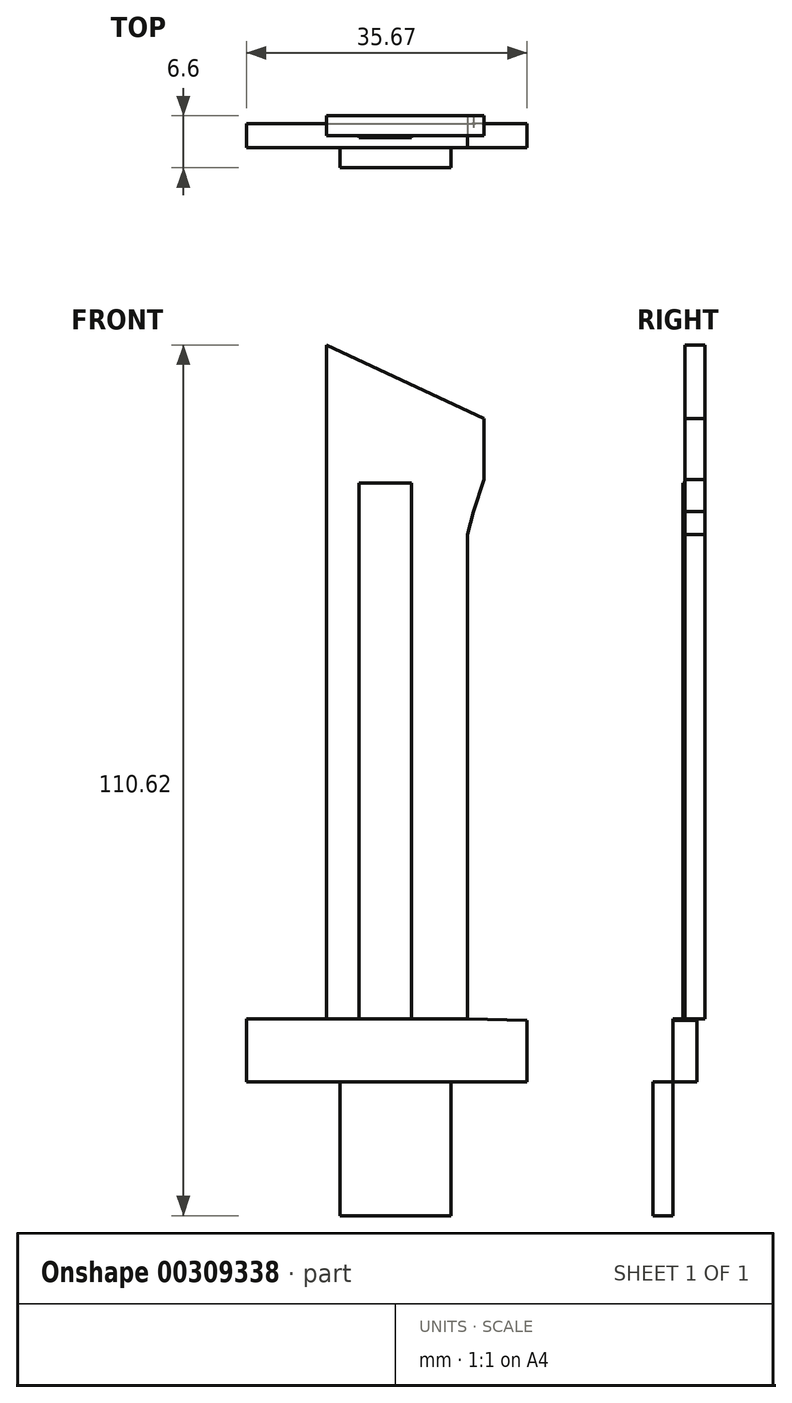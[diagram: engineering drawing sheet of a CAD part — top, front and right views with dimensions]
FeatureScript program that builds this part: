
annotation { "Feature Type Name" : "Feature", "Feature Type Description" : "" }
export const myFeature = defineFeature(function(context is Context, id is Id, definition is map)
    precondition{}
    {
        {
            var Q0;
            Q0=qCreatedBy(makeId("Front.planeOp"),FACE);
            var sketch = newSketch(context, id + "F0", { "sketchPlane" : qUnion([Q0])});
            skLineSegment(sketch, "E0", {"start": v(-34.4, 67.06) * mm, "end": v(-34.4, -7.2) * mm});
            skLineSegment(sketch, "E1", {"start": v(-34.4, 67.06) * mm, "end": v(-28.35, 67.06) * mm});
            skLineSegment(sketch, "E2", {"start": v(-28.35, 67.06) * mm, "end": v(-28.35, -7.2) * mm});
            skLineSegment(sketch, "E3", {"start": v(-28.35, -7.2) * mm, "end": v(-34.4, -7.2) * mm});
            skLineSegment(sketch, "E4", {"start": v(-41.36, -9.17) * mm, "end": v(-41.36, 76.44) * mm});
            skLineSegment(sketch, "E5", {"start": v(-41.36, 76.44) * mm, "end": v(-21.33, 67.06) * mm});
            skLineSegment(sketch, "E6", {"start": v(-21.33, 67.06) * mm, "end": v(-21.33, 59.31) * mm});
            skLineSegment(sketch, "E7", {"start": v(-21.33, 59.31) * mm, "end": v(-22.65, 55.26) * mm});
            skLineSegment(sketch, "E8", {"start": v(-22.65, 55.26) * mm, "end": v(-23.42, 52.35) * mm});
            skLineSegment(sketch, "E9", {"start": v(-23.42, 52.35) * mm, "end": v(-23.42, 50.2) * mm});
            skLineSegment(sketch, "E10", {"start": v(-23.42, 50.2) * mm, "end": v(-23.42, -9.17) * mm});
            skLineSegment(sketch, "E11", {"start": v(-41.36, -9.17) * mm, "end": v(-23.42, -9.17) * mm});
            skSolve(sketch);
        }
        {
            var Q0;
            Q0=makeQuery(id+"F0.imprint","IMPRINT",FACE,{"disambiguationData":[TD([[makeQuery(id+"F0.imprint","IMPRINT",EDGE,{"derivedFrom":sQuery(id+"F0.wireOp",EDGE,"E0")}),1.0]])]});
            var Q1;
            Q1=makeQuery(id+"F0.imprint","IMPRINT",FACE,{"disambiguationData":[TD([[makeQuery(id+"F0.imprint","IMPRINT",EDGE,{"derivedFrom":sQuery(id+"F0.wireOp",EDGE,"E0")}),-1.0]])]});
            extrude(context, id + "F1", {"entities" : qUnion([Q0, Q1]), "oppositeDirection" : true, "depth" : 2.54 * mm});
        }
        {
            var Q0;
            Q0=makeQuery(id+"F1.opExtrude","CAP_FACE",FACE,{"disambiguationData":[OSD([sQuery(id+"F0.wireOp",EDGE,"E4"),sQuery(id+"F0.wireOp",EDGE,"E5"),sQuery(id+"F0.wireOp",EDGE,"E6"),sQuery(id+"F0.wireOp",EDGE,"E7"),sQuery(id+"F0.wireOp",EDGE,"E8"),sQuery(id+"F0.wireOp",EDGE,"E9"),sQuery(id+"F0.wireOp",EDGE,"E10"),sQuery(id+"F0.wireOp",EDGE,"E11")])],"isStart":true});
            var sketch = newSketch(context, id + "F2", { "sketchPlane" : qUnion([Q0])});
            skLineSegment(sketch, "E12", {"start": v(-41.36, -9.17) * mm, "end": v(-51.52, -9.17) * mm});
            skLineSegment(sketch, "E13", {"start": v(-51.52, -9.17) * mm, "end": v(-51.52, -17.18) * mm});
            skLineSegment(sketch, "E14", {"start": v(-51.89, -17.18) * mm, "end": v(-15.85, -17.18) * mm});
            skLineSegment(sketch, "E15", {"start": v(-15.85, -17.18) * mm, "end": v(-15.85, -9.17) * mm});
            skLineSegment(sketch, "E16", {"start": v(-15.85, -9.4) * mm, "end": v(-23.42, -9.17) * mm});
            skSolve(sketch);
        }
        {
            var Q0;
            Q0=makeQuery(id+"F2.imprint","IMPRINT",FACE,{"disambiguationData":[TD([[makeQuery(id+"F2.imprint","IMPRINT",EDGE,{"derivedFrom":sQuery(id+"F2.wireOp",EDGE,"E12")}),1.0]])]});
            extrude(context, id + "F3", {"entities" : qUnion([Q0]), "operationType" : NewBodyOperationType.ADD, "endBound" : BoundingType.SYMMETRIC, "depth" : 3.05 * mm});
        }
        {
            var Q0;
            Q0=makeQuery(id+"F3.opExtrude","CAP_FACE",FACE,{"disambiguationData":[OSD([sQuery(id+"F0.wireOp",EDGE,"E11"),sQuery(id+"F2.wireOp",EDGE,"E12"),sQuery(id+"F2.wireOp",EDGE,"E13"),sQuery(id+"F2.wireOp",EDGE,"E14"),sQuery(id+"F2.wireOp",EDGE,"E15"),sQuery(id+"F2.wireOp",EDGE,"E16")])],"isStart":false});
            var sketch = newSketch(context, id + "F4", { "sketchPlane" : qUnion([Q0])});
            skLineSegment(sketch, "E17", {"start": v(-39.63, -17.18) * mm, "end": v(-39.63, -34.18) * mm});
            skLineSegment(sketch, "E18", {"start": v(-25.51, -34.18) * mm, "end": v(-25.51, -17.18) * mm});
            skLineSegment(sketch, "E19", {"start": v(-25.51, -17.18) * mm, "end": v(-39.63, -17.18) * mm});
            skLineSegment(sketch, "E20", {"start": v(-39.63, -34.18) * mm, "end": v(-25.51, -34.18) * mm});
            skSolve(sketch);
        }
        {
            var Q0;
            Q0=makeQuery(id+"F4.imprint","IMPRINT",FACE,{"disambiguationData":[TD([[makeQuery(id+"F4.imprint","IMPRINT",EDGE,{"derivedFrom":sQuery(id+"F4.wireOp",EDGE,"E17")}),1.0]])]});
            extrude(context, id + "F5", {"entities" : qUnion([Q0]), "depth" : 2.54 * mm});
        }
        {
            var Q0;
            Q0=makeQuery(id+"F1.opExtrude","CAP_FACE",FACE,{"disambiguationData":[OSD([sQuery(id+"F0.wireOp",EDGE,"E4"),sQuery(id+"F0.wireOp",EDGE,"E5"),sQuery(id+"F0.wireOp",EDGE,"E6"),sQuery(id+"F0.wireOp",EDGE,"E7"),sQuery(id+"F0.wireOp",EDGE,"E8"),sQuery(id+"F0.wireOp",EDGE,"E9"),sQuery(id+"F0.wireOp",EDGE,"E10"),sQuery(id+"F0.wireOp",EDGE,"E11")])],"isStart":true});
            var sketch = newSketch(context, id + "F6", { "sketchPlane" : qUnion([Q0])});
            skLineSegment(sketch, "E21", {"start": v(-37.18, 58.92) * mm, "end": v(-37.18, 18.85) * mm});
            skLineSegment(sketch, "E22", {"start": v(-30.55, 18.85) * mm, "end": v(-30.55, 58.92) * mm});
            skLineSegment(sketch, "E23", {"start": v(-37.18, 58.92) * mm, "end": v(-30.55, 58.92) * mm});
            skLineSegment(sketch, "E24", {"start": v(-37.18, 18.85) * mm, "end": v(-37.18, 3.7) * mm});
            skLineSegment(sketch, "E25", {"start": v(-30.55, 18.85) * mm, "end": v(-30.55, 15.45) * mm});
            skLineSegment(sketch, "E26", {"start": v(-30.55, 15.45) * mm, "end": v(-30.55, 3.7) * mm});
            skLineSegment(sketch, "E27", {"start": v(-37.18, 3.7) * mm, "end": v(-37.18, -9.17) * mm});
            skLineSegment(sketch, "E28", {"start": v(-30.55, 3.7) * mm, "end": v(-30.55, -9.17) * mm});
            skLineSegment(sketch, "E29", {"start": v(-37.18, -9.17) * mm, "end": v(-30.55, -9.17) * mm});
            skSolve(sketch);
        }
        {
            var Q0;
            Q0=makeQuery(id+"F6.imprint","IMPRINT",FACE,{"disambiguationData":[TD([[makeQuery(id+"F6.imprint","IMPRINT",EDGE,{"derivedFrom":sQuery(id+"F6.wireOp",EDGE,"E21")}),1.0]])]});
            extrude(context, id + "F7", {"entities" : qUnion([Q0]), "depth" : 0.25 * mm});
        }
    });
